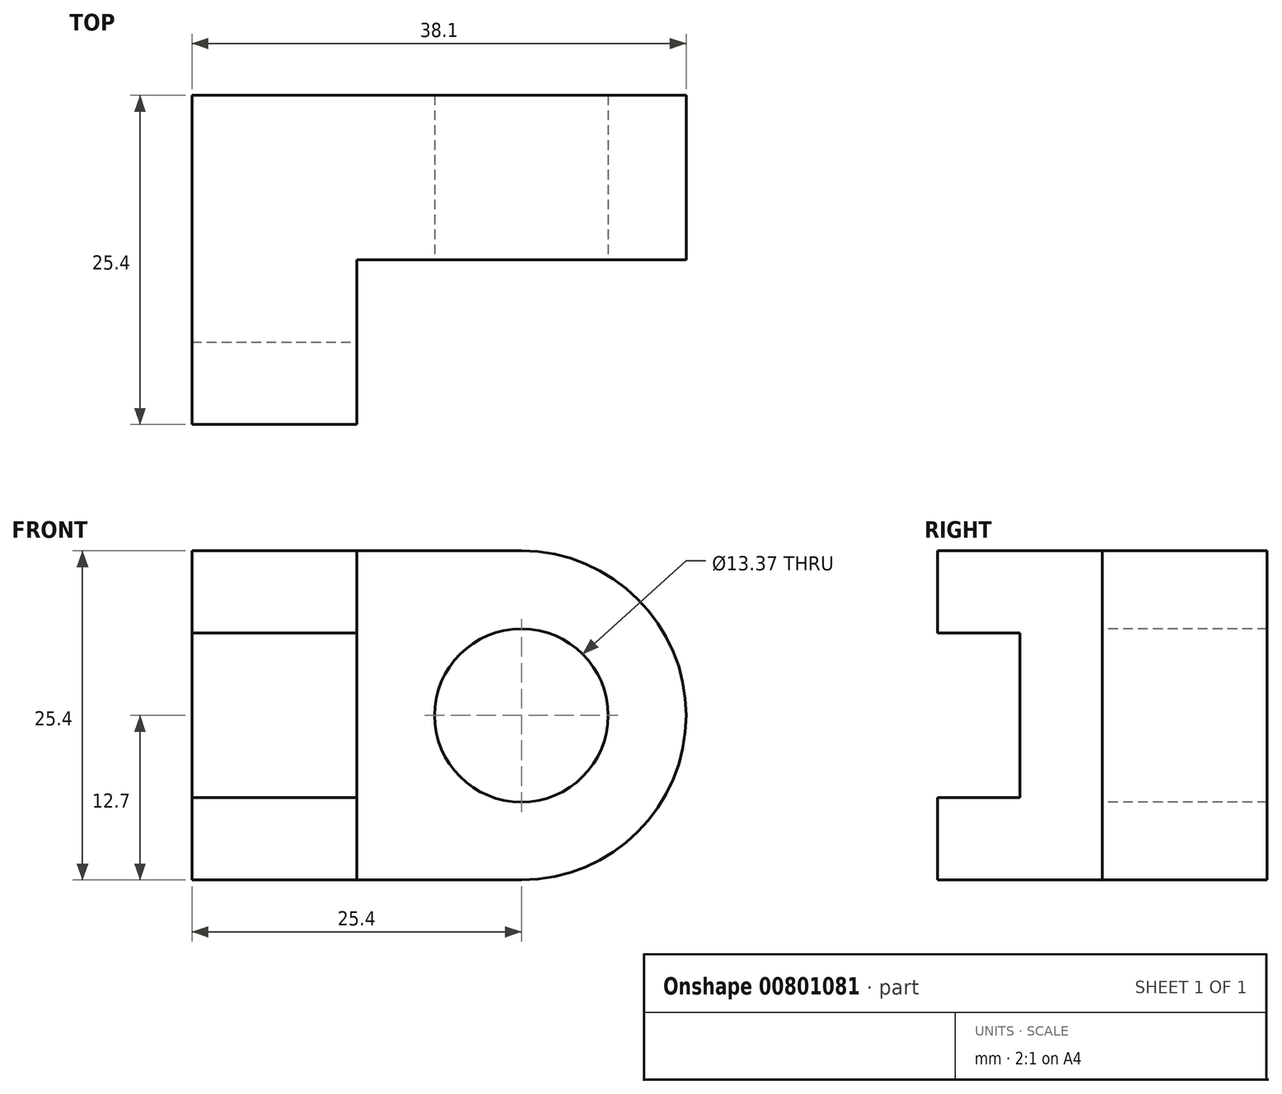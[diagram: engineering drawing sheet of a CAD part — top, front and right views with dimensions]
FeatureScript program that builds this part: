
annotation { "Feature Type Name" : "Feature", "Feature Type Description" : "" }
export const myFeature = defineFeature(function(context is Context, id is Id, definition is map)
    precondition{}
    {
        {
            var Q0;
            Q0=qCreatedBy(makeId("Top.planeOp"),FACE);
            var sketch = newSketch(context, id + "F0", { "sketchPlane" : qUnion([Q0])});
            skLineSegment(sketch, "E0", {"start": v(0, 0) * mm, "end": v(12.7, 0) * mm});
            skLineSegment(sketch, "E1", {"start": v(0, 0) * mm, "end": v(0, 25.4) * mm});
            skLineSegment(sketch, "E2", {"start": v(0, 25.4) * mm, "end": v(25.4, 25.4) * mm});
            skLineSegment(sketch, "E3", {"start": v(25.4, 25.4) * mm, "end": v(25.4, 12.7) * mm});
            skLineSegment(sketch, "E4", {"start": v(25.4, 12.7) * mm, "end": v(12.7, 12.7) * mm});
            skPoint(sketch, "E4.endSnap0", {"position": v(12.7, 25.4) * mm});
            skLineSegment(sketch, "E5", {"start": v(12.7, 12.7) * mm, "end": v(12.7, 0) * mm});
            skSolve(sketch);
        }
        {
            var Q0;
            Q0=makeQuery(id+"F0.imprint","IMPRINT",FACE,{"disambiguationData":[TD([[makeQuery(id+"F0.imprint","IMPRINT",EDGE,{"derivedFrom":sQuery(id+"F0.wireOp",EDGE,"E0")}),1.0]])]});
            extrude(context, id + "F1", {"entities" : qUnion([Q0]), "depth" : 25.4 * mm, "offsetDistance" : 25.4 * mm});
        }
        {
            var Q0;
            Q0=makeQuery(id+"F1.opExtrude","SWEPT_FACE",FACE,{"disambiguationData":[OSD([sQuery(id+"F0.wireOp",EDGE,"E5")])]});
            var sketch = newSketch(context, id + "F2", { "sketchPlane" : qUnion([Q0])});
            skLineSegment(sketch, "E6", {"start": v(0, 0) * mm, "end": v(0, 6.35) * mm});
            skLineSegment(sketch, "E7", {"start": v(0, 6.35) * mm, "end": v(6.35, 6.35) * mm});
            skLineSegment(sketch, "E8", {"start": v(6.35, 6.35) * mm, "end": v(6.35, 19.05) * mm});
            skLineSegment(sketch, "E9", {"start": v(6.35, 19.05) * mm, "end": v(0, 19.05) * mm});
            skLineSegment(sketch, "E10", {"start": v(0, 6.35) * mm, "end": v(0, 19.05) * mm});
            skSolve(sketch);
        }
        {
            var Q0;
            Q0=makeQuery(id+"F2.imprint","IMPRINT",FACE,{"disambiguationData":[TD([[makeQuery(id+"F2.imprint","IMPRINT",EDGE,{"derivedFrom":sQuery(id+"F2.wireOp",EDGE,"E7")}),1.0]])]});
            extrude(context, id + "F3", {"entities" : qUnion([Q0]), "operationType" : NewBodyOperationType.REMOVE, "oppositeDirection" : true, "depth" : 25.4 * mm, "offsetDistance" : 25.4 * mm});
        }
        {
            var Q0;
            Q0=makeQuery(id+"F1.opExtrude","SWEPT_FACE",FACE,{"disambiguationData":[OSD([sQuery(id+"F0.wireOp",EDGE,"E4")])]});
            var sketch = newSketch(context, id + "F4", { "sketchPlane" : qUnion([Q0])});
            skArc(sketch, "E11", {"start": v(25.4, 0) * mm, "mid": v(38.1, 12.7) * mm, "end": v(25.4, 25.4) * mm});
            skSolve(sketch);
        }
        {
            var Q0;
            Q0=makeQuery(id+"F4.imprint","IMPRINT",FACE,{"disambiguationData":[TD([[makeQuery(id+"F4.imprint","IMPRINT",EDGE,{"derivedFrom":sQuery(id+"F4.wireOp",EDGE,"E11")}),1.0]])]});
            extrude(context, id + "F5", {"entities" : qUnion([Q0]), "operationType" : NewBodyOperationType.ADD, "oppositeDirection" : true, "depth" : 12.7 * mm, "offsetDistance" : 25.4 * mm});
        }
        {
            var Q0;
            {var subQ0=sQuery(id+"F0.wireOp",EDGE,"E4");Q0=makeQuery(id+"F5.boolean.opBoolean","MERGE",FACE,{"derivedFrom":[makeQuery(id+"F1.opExtrude","SWEPT_FACE",FACE,{"disambiguationData":[OSD([subQ0])]}),makeQuery(id+"F5.opExtrude","CAP_FACE",FACE,{"disambiguationData":[OSD([sQuery(id+"F0.wireOp",EDGE,"E3"),subQ0,sQuery(id+"F4.wireOp",EDGE,"E11")])],"isStart":true})]});}
            var sketch = newSketch(context, id + "F6", { "sketchPlane" : qUnion([Q0])});
            skLineSegment(sketch, "E12", {"start": v(12.7, 12.7) * mm, "end": v(25.4, 12.7) * mm, "construction": true});
            skCircle(sketch, "E13", {"center": v(25.4, 12.7) * mm, "radius": 6.69 * mm});
            skSolve(sketch);
        }
        {
            var Q0;
            Q0=makeQuery(id+"F6.imprint","IMPRINT",FACE,{"disambiguationData":[TD([[makeQuery(id+"F6.imprint","IMPRINT",EDGE,{"derivedFrom":sQuery(id+"F6.wireOp",EDGE,"E13")}),1.0]])]});
            extrude(context, id + "F7", {"entities" : qUnion([Q0]), "operationType" : NewBodyOperationType.REMOVE, "oppositeDirection" : true, "depth" : 25.4 * mm, "offsetDistance" : 25.4 * mm});
        }
    });
